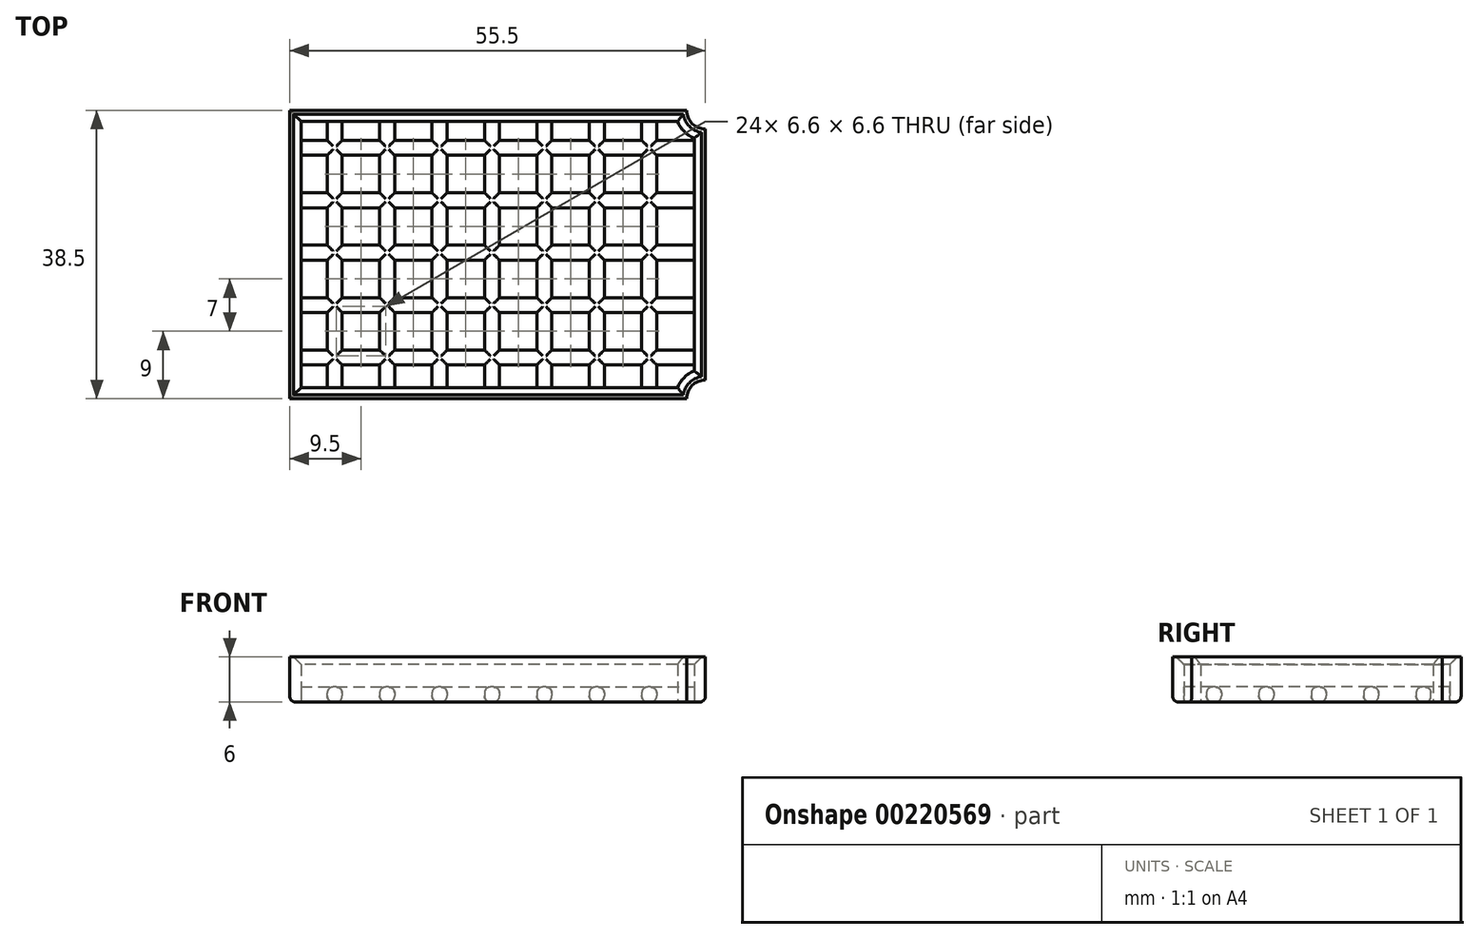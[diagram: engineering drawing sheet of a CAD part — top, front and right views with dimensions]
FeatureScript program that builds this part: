
annotation { "Feature Type Name" : "Feature", "Feature Type Description" : "" }
export const myFeature = defineFeature(function(context is Context, id is Id, definition is map)
    precondition{}
    {
        {
            var Q0;
            Q0=qCreatedBy(makeId("Top.planeOp"),FACE);
            var sketch = newSketch(context, id + "F0", { "sketchPlane" : qUnion([Q0])});
            skLineSegment(sketch, "E0.bottom", {"start": v(0, 38.5) * mm, "end": v(55.5, 38.5) * mm});
            skLineSegment(sketch, "E0.top", {"start": v(0, 0) * mm, "end": v(55.5, 0) * mm});
            skLineSegment(sketch, "E0.left", {"start": v(0, 38.5) * mm, "end": v(0, 0) * mm});
            skLineSegment(sketch, "E0.right", {"start": v(55.5, 38.5) * mm, "end": v(55.5, 0) * mm});
            skSolve(sketch);
        }
        {
            var Q0;
            Q0=qSketchRegion(id+"F0",true);
            extrude(context, id + "F1", {"entities" : qUnion([Q0]), "oppositeDirection" : true, "depth" : 2 * mm});
        }
        {
            var Q0;
            Q0=makeQuery(id+"F1.opExtrude","CAP_FACE",FACE,{"disambiguationData":[OSD([sQuery(id+"F0.wireOp",EDGE,"E0.bottom"),sQuery(id+"F0.wireOp",EDGE,"E0.top"),sQuery(id+"F0.wireOp",EDGE,"E0.left"),sQuery(id+"F0.wireOp",EDGE,"E0.right")])],"isStart":true});
            var sketch = newSketch(context, id + "F2", { "sketchPlane" : qUnion([Q0])});
            skLineSegment(sketch, "E1.bottom", {"start": v(0, 39.5) * mm, "end": v(5, 39.5) * mm});
            skLineSegment(sketch, "E1.top", {"start": v(0, 34.5) * mm, "end": v(5, 34.5) * mm});
            skLineSegment(sketch, "E1.left", {"start": v(0, 39.5) * mm, "end": v(0, 34.5) * mm});
            skLineSegment(sketch, "E1.right", {"start": v(5, 39.5) * mm, "end": v(5, 34.5) * mm});
            skLineSegment(sketch, "E2.0.1.0", {"start": v(0, 32.5) * mm, "end": v(5, 32.5) * mm});
            skLineSegment(sketch, "E2.0.1.1", {"start": v(0, 27.5) * mm, "end": v(5, 27.5) * mm});
            skLineSegment(sketch, "E2.0.1.2", {"start": v(0, 32.5) * mm, "end": v(0, 27.5) * mm});
            skLineSegment(sketch, "E2.0.1.3", {"start": v(5, 32.5) * mm, "end": v(5, 27.5) * mm});
            skLineSegment(sketch, "E2.0.2.0", {"start": v(0, 25.5) * mm, "end": v(5, 25.5) * mm});
            skLineSegment(sketch, "E2.0.2.1", {"start": v(0, 20.5) * mm, "end": v(5, 20.5) * mm});
            skLineSegment(sketch, "E2.0.2.2", {"start": v(0, 25.5) * mm, "end": v(0, 20.5) * mm});
            skLineSegment(sketch, "E2.0.2.3", {"start": v(5, 25.5) * mm, "end": v(5, 20.5) * mm});
            skLineSegment(sketch, "E2.0.3.0", {"start": v(0, 18.5) * mm, "end": v(5, 18.5) * mm});
            skLineSegment(sketch, "E2.0.3.1", {"start": v(0, 13.5) * mm, "end": v(5, 13.5) * mm});
            skLineSegment(sketch, "E2.0.3.2", {"start": v(0, 18.5) * mm, "end": v(0, 13.5) * mm});
            skLineSegment(sketch, "E2.0.3.3", {"start": v(5, 18.5) * mm, "end": v(5, 13.5) * mm});
            skLineSegment(sketch, "E2.0.4.0", {"start": v(0, 11.5) * mm, "end": v(5, 11.5) * mm});
            skLineSegment(sketch, "E2.0.4.1", {"start": v(0, 6.5) * mm, "end": v(5, 6.5) * mm});
            skLineSegment(sketch, "E2.0.4.2", {"start": v(0, 11.5) * mm, "end": v(0, 6.5) * mm});
            skLineSegment(sketch, "E2.0.4.3", {"start": v(5, 11.5) * mm, "end": v(5, 6.5) * mm});
            skLineSegment(sketch, "E2.0.5.0", {"start": v(0, 4.5) * mm, "end": v(5, 4.5) * mm});
            skLineSegment(sketch, "E2.0.5.1", {"start": v(0, -0.5) * mm, "end": v(5, -0.5) * mm});
            skLineSegment(sketch, "E2.0.5.2", {"start": v(0, 4.5) * mm, "end": v(0, -0.5) * mm});
            skLineSegment(sketch, "E2.0.5.3", {"start": v(5, 4.5) * mm, "end": v(5, -0.5) * mm});
            skLineSegment(sketch, "E2.1.0.0", {"start": v(7, 39.5) * mm, "end": v(12, 39.5) * mm});
            skLineSegment(sketch, "E2.1.0.1", {"start": v(7, 34.5) * mm, "end": v(12, 34.5) * mm});
            skLineSegment(sketch, "E2.1.0.2", {"start": v(7, 39.5) * mm, "end": v(7, 34.5) * mm});
            skLineSegment(sketch, "E2.1.0.3", {"start": v(12, 39.5) * mm, "end": v(12, 34.5) * mm});
            skLineSegment(sketch, "E2.1.1.0", {"start": v(7, 32.5) * mm, "end": v(12, 32.5) * mm});
            skLineSegment(sketch, "E2.1.1.1", {"start": v(7, 27.5) * mm, "end": v(12, 27.5) * mm});
            skLineSegment(sketch, "E2.1.1.2", {"start": v(7, 32.5) * mm, "end": v(7, 27.5) * mm});
            skLineSegment(sketch, "E2.1.1.3", {"start": v(12, 32.5) * mm, "end": v(12, 27.5) * mm});
            skLineSegment(sketch, "E2.1.2.0", {"start": v(7, 25.5) * mm, "end": v(12, 25.5) * mm});
            skLineSegment(sketch, "E2.1.2.1", {"start": v(7, 20.5) * mm, "end": v(12, 20.5) * mm});
            skLineSegment(sketch, "E2.1.2.2", {"start": v(7, 25.5) * mm, "end": v(7, 20.5) * mm});
            skLineSegment(sketch, "E2.1.2.3", {"start": v(12, 25.5) * mm, "end": v(12, 20.5) * mm});
            skLineSegment(sketch, "E2.1.3.0", {"start": v(7, 18.5) * mm, "end": v(12, 18.5) * mm});
            skLineSegment(sketch, "E2.1.3.1", {"start": v(7, 13.5) * mm, "end": v(12, 13.5) * mm});
            skLineSegment(sketch, "E2.1.3.2", {"start": v(7, 18.5) * mm, "end": v(7, 13.5) * mm});
            skLineSegment(sketch, "E2.1.3.3", {"start": v(12, 18.5) * mm, "end": v(12, 13.5) * mm});
            skLineSegment(sketch, "E2.1.4.0", {"start": v(7, 11.5) * mm, "end": v(12, 11.5) * mm});
            skLineSegment(sketch, "E2.1.4.1", {"start": v(7, 6.5) * mm, "end": v(12, 6.5) * mm});
            skLineSegment(sketch, "E2.1.4.2", {"start": v(7, 11.5) * mm, "end": v(7, 6.5) * mm});
            skLineSegment(sketch, "E2.1.4.3", {"start": v(12, 11.5) * mm, "end": v(12, 6.5) * mm});
            skLineSegment(sketch, "E2.1.5.0", {"start": v(7, 4.5) * mm, "end": v(12, 4.5) * mm});
            skLineSegment(sketch, "E2.1.5.1", {"start": v(7, -0.5) * mm, "end": v(12, -0.5) * mm});
            skLineSegment(sketch, "E2.1.5.2", {"start": v(7, 4.5) * mm, "end": v(7, -0.5) * mm});
            skLineSegment(sketch, "E2.1.5.3", {"start": v(12, 4.5) * mm, "end": v(12, -0.5) * mm});
            skLineSegment(sketch, "E2.2.0.0", {"start": v(14, 39.5) * mm, "end": v(19, 39.5) * mm});
            skLineSegment(sketch, "E2.2.0.1", {"start": v(14, 34.5) * mm, "end": v(19, 34.5) * mm});
            skLineSegment(sketch, "E2.2.0.2", {"start": v(14, 39.5) * mm, "end": v(14, 34.5) * mm});
            skLineSegment(sketch, "E2.2.0.3", {"start": v(19, 39.5) * mm, "end": v(19, 34.5) * mm});
            skLineSegment(sketch, "E2.2.1.0", {"start": v(14, 32.5) * mm, "end": v(19, 32.5) * mm});
            skLineSegment(sketch, "E2.2.1.1", {"start": v(14, 27.5) * mm, "end": v(19, 27.5) * mm});
            skLineSegment(sketch, "E2.2.1.2", {"start": v(14, 32.5) * mm, "end": v(14, 27.5) * mm});
            skLineSegment(sketch, "E2.2.1.3", {"start": v(19, 32.5) * mm, "end": v(19, 27.5) * mm});
            skLineSegment(sketch, "E2.2.2.0", {"start": v(14, 25.5) * mm, "end": v(19, 25.5) * mm});
            skLineSegment(sketch, "E2.2.2.1", {"start": v(14, 20.5) * mm, "end": v(19, 20.5) * mm});
            skLineSegment(sketch, "E2.2.2.2", {"start": v(14, 25.5) * mm, "end": v(14, 20.5) * mm});
            skLineSegment(sketch, "E2.2.2.3", {"start": v(19, 25.5) * mm, "end": v(19, 20.5) * mm});
            skLineSegment(sketch, "E2.2.3.0", {"start": v(14, 18.5) * mm, "end": v(19, 18.5) * mm});
            skLineSegment(sketch, "E2.2.3.1", {"start": v(14, 13.5) * mm, "end": v(19, 13.5) * mm});
            skLineSegment(sketch, "E2.2.3.2", {"start": v(14, 18.5) * mm, "end": v(14, 13.5) * mm});
            skLineSegment(sketch, "E2.2.3.3", {"start": v(19, 18.5) * mm, "end": v(19, 13.5) * mm});
            skLineSegment(sketch, "E2.2.4.0", {"start": v(14, 11.5) * mm, "end": v(19, 11.5) * mm});
            skLineSegment(sketch, "E2.2.4.1", {"start": v(14, 6.5) * mm, "end": v(19, 6.5) * mm});
            skLineSegment(sketch, "E2.2.4.2", {"start": v(14, 11.5) * mm, "end": v(14, 6.5) * mm});
            skLineSegment(sketch, "E2.2.4.3", {"start": v(19, 11.5) * mm, "end": v(19, 6.5) * mm});
            skLineSegment(sketch, "E2.2.5.0", {"start": v(14, 4.5) * mm, "end": v(19, 4.5) * mm});
            skLineSegment(sketch, "E2.2.5.1", {"start": v(14, -0.5) * mm, "end": v(19, -0.5) * mm});
            skLineSegment(sketch, "E2.2.5.2", {"start": v(14, 4.5) * mm, "end": v(14, -0.5) * mm});
            skLineSegment(sketch, "E2.2.5.3", {"start": v(19, 4.5) * mm, "end": v(19, -0.5) * mm});
            skLineSegment(sketch, "E2.3.0.0", {"start": v(21, 39.5) * mm, "end": v(26, 39.5) * mm});
            skLineSegment(sketch, "E2.3.0.1", {"start": v(21, 34.5) * mm, "end": v(26, 34.5) * mm});
            skLineSegment(sketch, "E2.3.0.2", {"start": v(21, 39.5) * mm, "end": v(21, 34.5) * mm});
            skLineSegment(sketch, "E2.3.0.3", {"start": v(26, 39.5) * mm, "end": v(26, 34.5) * mm});
            skLineSegment(sketch, "E2.3.1.0", {"start": v(21, 32.5) * mm, "end": v(26, 32.5) * mm});
            skLineSegment(sketch, "E2.3.1.1", {"start": v(21, 27.5) * mm, "end": v(26, 27.5) * mm});
            skLineSegment(sketch, "E2.3.1.2", {"start": v(21, 32.5) * mm, "end": v(21, 27.5) * mm});
            skLineSegment(sketch, "E2.3.1.3", {"start": v(26, 32.5) * mm, "end": v(26, 27.5) * mm});
            skLineSegment(sketch, "E2.3.2.0", {"start": v(21, 25.5) * mm, "end": v(26, 25.5) * mm});
            skLineSegment(sketch, "E2.3.2.1", {"start": v(21, 20.5) * mm, "end": v(26, 20.5) * mm});
            skLineSegment(sketch, "E2.3.2.2", {"start": v(21, 25.5) * mm, "end": v(21, 20.5) * mm});
            skLineSegment(sketch, "E2.3.2.3", {"start": v(26, 25.5) * mm, "end": v(26, 20.5) * mm});
            skLineSegment(sketch, "E2.3.3.0", {"start": v(21, 18.5) * mm, "end": v(26, 18.5) * mm});
            skLineSegment(sketch, "E2.3.3.1", {"start": v(21, 13.5) * mm, "end": v(26, 13.5) * mm});
            skLineSegment(sketch, "E2.3.3.2", {"start": v(21, 18.5) * mm, "end": v(21, 13.5) * mm});
            skLineSegment(sketch, "E2.3.3.3", {"start": v(26, 18.5) * mm, "end": v(26, 13.5) * mm});
            skLineSegment(sketch, "E2.3.4.0", {"start": v(21, 11.5) * mm, "end": v(26, 11.5) * mm});
            skLineSegment(sketch, "E2.3.4.1", {"start": v(21, 6.5) * mm, "end": v(26, 6.5) * mm});
            skLineSegment(sketch, "E2.3.4.2", {"start": v(21, 11.5) * mm, "end": v(21, 6.5) * mm});
            skLineSegment(sketch, "E2.3.4.3", {"start": v(26, 11.5) * mm, "end": v(26, 6.5) * mm});
            skLineSegment(sketch, "E2.3.5.0", {"start": v(21, 4.5) * mm, "end": v(26, 4.5) * mm});
            skLineSegment(sketch, "E2.3.5.1", {"start": v(21, -0.5) * mm, "end": v(26, -0.5) * mm});
            skLineSegment(sketch, "E2.3.5.2", {"start": v(21, 4.5) * mm, "end": v(21, -0.5) * mm});
            skLineSegment(sketch, "E2.3.5.3", {"start": v(26, 4.5) * mm, "end": v(26, -0.5) * mm});
            skLineSegment(sketch, "E2.4.0.0", {"start": v(28, 39.5) * mm, "end": v(33, 39.5) * mm});
            skLineSegment(sketch, "E2.4.0.1", {"start": v(28, 34.5) * mm, "end": v(33, 34.5) * mm});
            skLineSegment(sketch, "E2.4.0.2", {"start": v(28, 39.5) * mm, "end": v(28, 34.5) * mm});
            skLineSegment(sketch, "E2.4.0.3", {"start": v(33, 39.5) * mm, "end": v(33, 34.5) * mm});
            skLineSegment(sketch, "E2.4.1.0", {"start": v(28, 32.5) * mm, "end": v(33, 32.5) * mm});
            skLineSegment(sketch, "E2.4.1.1", {"start": v(28, 27.5) * mm, "end": v(33, 27.5) * mm});
            skLineSegment(sketch, "E2.4.1.2", {"start": v(28, 32.5) * mm, "end": v(28, 27.5) * mm});
            skLineSegment(sketch, "E2.4.1.3", {"start": v(33, 32.5) * mm, "end": v(33, 27.5) * mm});
            skLineSegment(sketch, "E2.4.2.0", {"start": v(28, 25.5) * mm, "end": v(33, 25.5) * mm});
            skLineSegment(sketch, "E2.4.2.1", {"start": v(28, 20.5) * mm, "end": v(33, 20.5) * mm});
            skLineSegment(sketch, "E2.4.2.2", {"start": v(28, 25.5) * mm, "end": v(28, 20.5) * mm});
            skLineSegment(sketch, "E2.4.2.3", {"start": v(33, 25.5) * mm, "end": v(33, 20.5) * mm});
            skLineSegment(sketch, "E2.4.3.0", {"start": v(28, 18.5) * mm, "end": v(33, 18.5) * mm});
            skLineSegment(sketch, "E2.4.3.1", {"start": v(28, 13.5) * mm, "end": v(33, 13.5) * mm});
            skLineSegment(sketch, "E2.4.3.2", {"start": v(28, 18.5) * mm, "end": v(28, 13.5) * mm});
            skLineSegment(sketch, "E2.4.3.3", {"start": v(33, 18.5) * mm, "end": v(33, 13.5) * mm});
            skLineSegment(sketch, "E2.4.4.0", {"start": v(28, 11.5) * mm, "end": v(33, 11.5) * mm});
            skLineSegment(sketch, "E2.4.4.1", {"start": v(28, 6.5) * mm, "end": v(33, 6.5) * mm});
            skLineSegment(sketch, "E2.4.4.2", {"start": v(28, 11.5) * mm, "end": v(28, 6.5) * mm});
            skLineSegment(sketch, "E2.4.4.3", {"start": v(33, 11.5) * mm, "end": v(33, 6.5) * mm});
            skLineSegment(sketch, "E2.4.5.0", {"start": v(28, 4.5) * mm, "end": v(33, 4.5) * mm});
            skLineSegment(sketch, "E2.4.5.1", {"start": v(28, -0.5) * mm, "end": v(33, -0.5) * mm});
            skLineSegment(sketch, "E2.4.5.2", {"start": v(28, 4.5) * mm, "end": v(28, -0.5) * mm});
            skLineSegment(sketch, "E2.4.5.3", {"start": v(33, 4.5) * mm, "end": v(33, -0.5) * mm});
            skLineSegment(sketch, "E2.5.0.0", {"start": v(35, 39.5) * mm, "end": v(40, 39.5) * mm});
            skLineSegment(sketch, "E2.5.0.1", {"start": v(35, 34.5) * mm, "end": v(40, 34.5) * mm});
            skLineSegment(sketch, "E2.5.0.2", {"start": v(35, 39.5) * mm, "end": v(35, 34.5) * mm});
            skLineSegment(sketch, "E2.5.0.3", {"start": v(40, 39.5) * mm, "end": v(40, 34.5) * mm});
            skLineSegment(sketch, "E2.5.1.0", {"start": v(35, 32.5) * mm, "end": v(40, 32.5) * mm});
            skLineSegment(sketch, "E2.5.1.1", {"start": v(35, 27.5) * mm, "end": v(40, 27.5) * mm});
            skLineSegment(sketch, "E2.5.1.2", {"start": v(35, 32.5) * mm, "end": v(35, 27.5) * mm});
            skLineSegment(sketch, "E2.5.1.3", {"start": v(40, 32.5) * mm, "end": v(40, 27.5) * mm});
            skLineSegment(sketch, "E2.5.2.0", {"start": v(35, 25.5) * mm, "end": v(40, 25.5) * mm});
            skLineSegment(sketch, "E2.5.2.1", {"start": v(35, 20.5) * mm, "end": v(40, 20.5) * mm});
            skLineSegment(sketch, "E2.5.2.2", {"start": v(35, 25.5) * mm, "end": v(35, 20.5) * mm});
            skLineSegment(sketch, "E2.5.2.3", {"start": v(40, 25.5) * mm, "end": v(40, 20.5) * mm});
            skLineSegment(sketch, "E2.5.3.0", {"start": v(35, 18.5) * mm, "end": v(40, 18.5) * mm});
            skLineSegment(sketch, "E2.5.3.1", {"start": v(35, 13.5) * mm, "end": v(40, 13.5) * mm});
            skLineSegment(sketch, "E2.5.3.2", {"start": v(35, 18.5) * mm, "end": v(35, 13.5) * mm});
            skLineSegment(sketch, "E2.5.3.3", {"start": v(40, 18.5) * mm, "end": v(40, 13.5) * mm});
            skLineSegment(sketch, "E2.5.4.0", {"start": v(35, 11.5) * mm, "end": v(40, 11.5) * mm});
            skLineSegment(sketch, "E2.5.4.1", {"start": v(35, 6.5) * mm, "end": v(40, 6.5) * mm});
            skLineSegment(sketch, "E2.5.4.2", {"start": v(35, 11.5) * mm, "end": v(35, 6.5) * mm});
            skLineSegment(sketch, "E2.5.4.3", {"start": v(40, 11.5) * mm, "end": v(40, 6.5) * mm});
            skLineSegment(sketch, "E2.5.5.0", {"start": v(35, 4.5) * mm, "end": v(40, 4.5) * mm});
            skLineSegment(sketch, "E2.5.5.1", {"start": v(35, -0.5) * mm, "end": v(40, -0.5) * mm});
            skLineSegment(sketch, "E2.5.5.2", {"start": v(35, 4.5) * mm, "end": v(35, -0.5) * mm});
            skLineSegment(sketch, "E2.5.5.3", {"start": v(40, 4.5) * mm, "end": v(40, -0.5) * mm});
            skLineSegment(sketch, "E2.6.0.0", {"start": v(42, 39.5) * mm, "end": v(47, 39.5) * mm});
            skLineSegment(sketch, "E2.6.0.1", {"start": v(42, 34.5) * mm, "end": v(47, 34.5) * mm});
            skLineSegment(sketch, "E2.6.0.2", {"start": v(42, 39.5) * mm, "end": v(42, 34.5) * mm});
            skLineSegment(sketch, "E2.6.0.3", {"start": v(47, 39.5) * mm, "end": v(47, 34.5) * mm});
            skLineSegment(sketch, "E2.6.1.0", {"start": v(42, 32.5) * mm, "end": v(47, 32.5) * mm});
            skLineSegment(sketch, "E2.6.1.1", {"start": v(42, 27.5) * mm, "end": v(47, 27.5) * mm});
            skLineSegment(sketch, "E2.6.1.2", {"start": v(42, 32.5) * mm, "end": v(42, 27.5) * mm});
            skLineSegment(sketch, "E2.6.1.3", {"start": v(47, 32.5) * mm, "end": v(47, 27.5) * mm});
            skLineSegment(sketch, "E2.6.2.0", {"start": v(42, 25.5) * mm, "end": v(47, 25.5) * mm});
            skLineSegment(sketch, "E2.6.2.1", {"start": v(42, 20.5) * mm, "end": v(47, 20.5) * mm});
            skLineSegment(sketch, "E2.6.2.2", {"start": v(42, 25.5) * mm, "end": v(42, 20.5) * mm});
            skLineSegment(sketch, "E2.6.2.3", {"start": v(47, 25.5) * mm, "end": v(47, 20.5) * mm});
            skLineSegment(sketch, "E2.6.3.0", {"start": v(42, 18.5) * mm, "end": v(47, 18.5) * mm});
            skLineSegment(sketch, "E2.6.3.1", {"start": v(42, 13.5) * mm, "end": v(47, 13.5) * mm});
            skLineSegment(sketch, "E2.6.3.2", {"start": v(42, 18.5) * mm, "end": v(42, 13.5) * mm});
            skLineSegment(sketch, "E2.6.3.3", {"start": v(47, 18.5) * mm, "end": v(47, 13.5) * mm});
            skLineSegment(sketch, "E2.6.4.0", {"start": v(42, 11.5) * mm, "end": v(47, 11.5) * mm});
            skLineSegment(sketch, "E2.6.4.1", {"start": v(42, 6.5) * mm, "end": v(47, 6.5) * mm});
            skLineSegment(sketch, "E2.6.4.2", {"start": v(42, 11.5) * mm, "end": v(42, 6.5) * mm});
            skLineSegment(sketch, "E2.6.4.3", {"start": v(47, 11.5) * mm, "end": v(47, 6.5) * mm});
            skLineSegment(sketch, "E2.6.5.0", {"start": v(42, 4.5) * mm, "end": v(47, 4.5) * mm});
            skLineSegment(sketch, "E2.6.5.1", {"start": v(42, -0.5) * mm, "end": v(47, -0.5) * mm});
            skLineSegment(sketch, "E2.6.5.2", {"start": v(42, 4.5) * mm, "end": v(42, -0.5) * mm});
            skLineSegment(sketch, "E2.6.5.3", {"start": v(47, 4.5) * mm, "end": v(47, -0.5) * mm});
            skLineSegment(sketch, "E2.7.0.0", {"start": v(49, 39.5) * mm, "end": v(54, 39.5) * mm});
            skLineSegment(sketch, "E2.7.0.1", {"start": v(49, 34.5) * mm, "end": v(54, 34.5) * mm});
            skLineSegment(sketch, "E2.7.0.2", {"start": v(49, 39.5) * mm, "end": v(49, 34.5) * mm});
            skLineSegment(sketch, "E2.7.0.3", {"start": v(54, 39.5) * mm, "end": v(54, 34.5) * mm});
            skLineSegment(sketch, "E2.7.1.0", {"start": v(49, 32.5) * mm, "end": v(54, 32.5) * mm});
            skLineSegment(sketch, "E2.7.1.1", {"start": v(49, 27.5) * mm, "end": v(54, 27.5) * mm});
            skLineSegment(sketch, "E2.7.1.2", {"start": v(49, 32.5) * mm, "end": v(49, 27.5) * mm});
            skLineSegment(sketch, "E2.7.1.3", {"start": v(54, 32.5) * mm, "end": v(54, 27.5) * mm});
            skLineSegment(sketch, "E2.7.2.0", {"start": v(49, 25.5) * mm, "end": v(54, 25.5) * mm});
            skLineSegment(sketch, "E2.7.2.1", {"start": v(49, 20.5) * mm, "end": v(54, 20.5) * mm});
            skLineSegment(sketch, "E2.7.2.2", {"start": v(49, 25.5) * mm, "end": v(49, 20.5) * mm});
            skLineSegment(sketch, "E2.7.2.3", {"start": v(54, 25.5) * mm, "end": v(54, 20.5) * mm});
            skLineSegment(sketch, "E2.7.3.0", {"start": v(49, 18.5) * mm, "end": v(54, 18.5) * mm});
            skLineSegment(sketch, "E2.7.3.1", {"start": v(49, 13.5) * mm, "end": v(54, 13.5) * mm});
            skLineSegment(sketch, "E2.7.3.2", {"start": v(49, 18.5) * mm, "end": v(49, 13.5) * mm});
            skLineSegment(sketch, "E2.7.3.3", {"start": v(54, 18.5) * mm, "end": v(54, 13.5) * mm});
            skLineSegment(sketch, "E2.7.4.0", {"start": v(49, 11.5) * mm, "end": v(54, 11.5) * mm});
            skLineSegment(sketch, "E2.7.4.1", {"start": v(49, 6.5) * mm, "end": v(54, 6.5) * mm});
            skLineSegment(sketch, "E2.7.4.2", {"start": v(49, 11.5) * mm, "end": v(49, 6.5) * mm});
            skLineSegment(sketch, "E2.7.4.3", {"start": v(54, 11.5) * mm, "end": v(54, 6.5) * mm});
            skLineSegment(sketch, "E2.7.5.0", {"start": v(49, 4.5) * mm, "end": v(54, 4.5) * mm});
            skLineSegment(sketch, "E2.7.5.1", {"start": v(49, -0.5) * mm, "end": v(54, -0.5) * mm});
            skLineSegment(sketch, "E2.7.5.2", {"start": v(49, 4.5) * mm, "end": v(49, -0.5) * mm});
            skLineSegment(sketch, "E2.7.5.3", {"start": v(54, 4.5) * mm, "end": v(54, -0.5) * mm});
            skLineSegment(sketch, "E2.direction1", {"start": v(0, 34.5) * mm, "end": v(7, 34.5) * mm, "construction": true});
            skLineSegment(sketch, "E2.direction2", {"start": v(0, 34.5) * mm, "end": v(0, 27.5) * mm, "construction": true});
            skLineSegment(sketch, "E3.bottom", {"start": v(54, 39.5) * mm, "end": v(58.15, 39.5) * mm});
            skLineSegment(sketch, "E3.top", {"start": v(54, 34.5) * mm, "end": v(58.15, 34.5) * mm});
            skLineSegment(sketch, "E3.right", {"start": v(58.15, 39.5) * mm, "end": v(58.15, 34.5) * mm});
            skLineSegment(sketch, "E4.1.0.0", {"start": v(54, 27.5) * mm, "end": v(58.15, 27.5) * mm});
            skLineSegment(sketch, "E4.1.0.1", {"start": v(58.15, 32.5) * mm, "end": v(58.15, 27.5) * mm});
            skLineSegment(sketch, "E4.1.0.2", {"start": v(54, 32.5) * mm, "end": v(58.15, 32.5) * mm});
            skLineSegment(sketch, "E4.2.0.0", {"start": v(54, 20.5) * mm, "end": v(58.15, 20.5) * mm});
            skLineSegment(sketch, "E4.2.0.1", {"start": v(58.15, 25.5) * mm, "end": v(58.15, 20.5) * mm});
            skLineSegment(sketch, "E4.2.0.2", {"start": v(54, 25.5) * mm, "end": v(58.15, 25.5) * mm});
            skLineSegment(sketch, "E4.3.0.0", {"start": v(54, 13.5) * mm, "end": v(58.15, 13.5) * mm});
            skLineSegment(sketch, "E4.3.0.1", {"start": v(58.15, 18.5) * mm, "end": v(58.15, 13.5) * mm});
            skLineSegment(sketch, "E4.3.0.2", {"start": v(54, 18.5) * mm, "end": v(58.15, 18.5) * mm});
            skLineSegment(sketch, "E4.4.0.0", {"start": v(54, 6.5) * mm, "end": v(58.15, 6.5) * mm});
            skLineSegment(sketch, "E4.4.0.1", {"start": v(58.15, 11.5) * mm, "end": v(58.15, 6.5) * mm});
            skLineSegment(sketch, "E4.4.0.2", {"start": v(54, 11.5) * mm, "end": v(58.15, 11.5) * mm});
            skLineSegment(sketch, "E4.5.0.0", {"start": v(54, -0.5) * mm, "end": v(58.15, -0.5) * mm});
            skLineSegment(sketch, "E4.5.0.1", {"start": v(58.15, 4.5) * mm, "end": v(58.15, -0.5) * mm});
            skLineSegment(sketch, "E4.5.0.2", {"start": v(54, 4.5) * mm, "end": v(58.15, 4.5) * mm});
            skLineSegment(sketch, "E4.direction1", {"start": v(54, 34.5) * mm, "end": v(54, 27.5) * mm, "construction": true});
            skSolve(sketch);
        }
        {
            var Q0;
            Q0=qSketchRegion(id+"F2",true);
            extrude(context, id + "F3", {"entities" : qUnion([Q0]), "operationType" : NewBodyOperationType.REMOVE, "endBound" : BoundingType.THROUGH_ALL, "oppositeDirection" : true, "depth" : 25 * mm});
        }
        {
            var Q0;
            Q0=makeQuery(id+"F1.opExtrude","CAP_FACE",FACE,{"disambiguationData":[OSD([sQuery(id+"F0.wireOp",EDGE,"E0.bottom"),sQuery(id+"F0.wireOp",EDGE,"E0.top"),sQuery(id+"F0.wireOp",EDGE,"E0.left"),sQuery(id+"F0.wireOp",EDGE,"E0.right")])],"isStart":false});
            var sketch = newSketch(context, id + "F4", { "sketchPlane" : qUnion([Q0])});
            skLineSegment(sketch, "E5.bottom", {"start": v(0, 0) * mm, "end": v(55.5, 0) * mm});
            skLineSegment(sketch, "E5.top", {"start": v(0, -38.5) * mm, "end": v(55.5, -38.5) * mm});
            skLineSegment(sketch, "E5.left", {"start": v(0, 0) * mm, "end": v(0, -38.5) * mm});
            skLineSegment(sketch, "E5.right", {"start": v(55.5, 0) * mm, "end": v(55.5, -38.5) * mm});
            skLineSegment(sketch, "E6.0", {"start": v(1.5, -1.5) * mm, "end": v(1.5, -37) * mm});
            skLineSegment(sketch, "E6.1", {"start": v(1.5, -1.5) * mm, "end": v(54, -1.5) * mm});
            skLineSegment(sketch, "E6.2", {"start": v(54, -1.5) * mm, "end": v(54, -37) * mm});
            skLineSegment(sketch, "E6.3", {"start": v(1.5, -37) * mm, "end": v(54, -37) * mm});
            skSolve(sketch);
        }
        {
            var Q0;
            Q0=makeQuery(id+"F1.opExtrude","CAP_FACE",FACE,{"disambiguationData":[OSD([sQuery(id+"F0.wireOp",EDGE,"E0.bottom"),sQuery(id+"F0.wireOp",EDGE,"E0.top"),sQuery(id+"F0.wireOp",EDGE,"E0.left"),sQuery(id+"F0.wireOp",EDGE,"E0.right")])],"isStart":true});
            var Q1;
            Q1=makeQuery(id+"F1.opExtrude","CAP_FACE",FACE,{"disambiguationData":[OSD([sQuery(id+"F0.wireOp",EDGE,"E0.bottom"),sQuery(id+"F0.wireOp",EDGE,"E0.top"),sQuery(id+"F0.wireOp",EDGE,"E0.left"),sQuery(id+"F0.wireOp",EDGE,"E0.right")])],"isStart":false});
            fillet(context, id + "F5", {"entities" : qUnion([Q0, Q1]), "radius" : 0.8 * mm, "defaultsChanged" : true, "vertexSettings" : [], "allowEdgeOverflow" : false});
        }
        {
            var Q0;
            Q0=qSketchRegion(id+"F4",true);
            extrude(context, id + "F6", {"entities" : qUnion([Q0]), "operationType" : NewBodyOperationType.ADD, "oppositeDirection" : true, "depth" : 6 * mm});
        }
        {
            var Q0;
            Q0=makeQuery(id+"F1.opExtrude","CAP_FACE",FACE,{"disambiguationData":[OSD([sQuery(id+"F0.wireOp",EDGE,"E0.bottom"),sQuery(id+"F0.wireOp",EDGE,"E0.top"),sQuery(id+"F0.wireOp",EDGE,"E0.left"),sQuery(id+"F0.wireOp",EDGE,"E0.right")])],"isStart":false});
            var sketch = newSketch(context, id + "F7", { "sketchPlane" : qUnion([Q0])});
            skArc(sketch, "E7", {"start": v(55.5, -34.5) * mm, "mid": v(52.67, -35.67) * mm, "end": v(51.5, -38.5) * mm});
            skArc(sketch, "E8", {"start": v(55.5, -4) * mm, "mid": v(52.67, -2.83) * mm, "end": v(51.5, 0) * mm});
            skLineSegment(sketch, "E9", {"start": v(55.5, -34.5) * mm, "end": v(55.5, -38.5) * mm});
            skLineSegment(sketch, "E10", {"start": v(55.5, -38.5) * mm, "end": v(51.5, -38.5) * mm});
            skLineSegment(sketch, "E11", {"start": v(55.5, 0) * mm, "end": v(55.5, -4) * mm});
            skLineSegment(sketch, "E12", {"start": v(55.5, 0) * mm, "end": v(51.5, 0) * mm});
            skSolve(sketch);
        }
        {
            var Q0;
            Q0 = qSketchRegion(id + "F7", true);
            var Q1;
            Q1=makeQuery(id+"F6.opExtrude","CAP_FACE",FACE,{"disambiguationData":[OSD([sQuery(id+"F4.wireOp",EDGE,"E5.bottom"),sQuery(id+"F4.wireOp",EDGE,"E5.top"),sQuery(id+"F4.wireOp",EDGE,"E5.left"),sQuery(id+"F4.wireOp",EDGE,"E5.right"),sQuery(id+"F4.wireOp",EDGE,"E6.0"),sQuery(id+"F4.wireOp",EDGE,"E6.1"),sQuery(id+"F4.wireOp",EDGE,"E6.2"),sQuery(id+"F4.wireOp",EDGE,"E6.3")])],"isStart":false});
            extrude(context, id + "F8", {"entities" : qUnion([Q0]), "operationType" : NewBodyOperationType.ADD, "endBound" : BoundingType.UP_TO_SURFACE, "oppositeDirection" : true, "depth" : 25 * mm, "endBoundEntityFace" : qUnion([Q1]), "offsetDistance" : 25 * mm});
        }
        {
            var Q0;
            Q0=makeQuery(id+"F1.opExtrude","CAP_FACE",FACE,{"disambiguationData":[OSD([sQuery(id+"F0.wireOp",EDGE,"E0.bottom"),sQuery(id+"F0.wireOp",EDGE,"E0.top"),sQuery(id+"F0.wireOp",EDGE,"E0.left"),sQuery(id+"F0.wireOp",EDGE,"E0.right")])],"isStart":false});
            var sketch = newSketch(context, id + "F9", { "sketchPlane" : qUnion([Q0])});
            skCircle(sketch, "E13", {"center": v(55.5, -38.5) * mm, "radius": 2.5 * mm});
            skCircle(sketch, "E14", {"center": v(55.5, 0) * mm, "radius": 2.5 * mm});
            skSolve(sketch);
        }
        {
            var Q0;
            Q0 = qSketchRegion(id + "F9", true);
            extrude(context, id + "F10", {"entities" : qUnion([Q0]), "operationType" : NewBodyOperationType.REMOVE, "oppositeDirection" : true, "depth" : 25 * mm, "offsetDistance" : 25 * mm});
        }
        {
            var Q0;
            Q0=makeQuery(id+"F6.opExtrude","CAP_EDGE",EDGE,{"disambiguationData":[OSD([sQuery(id+"F4.wireOp",EDGE,"E6.3")])],"isStart":false});
            var Q1;
            Q1=makeQuery(id+"F6.opExtrude","CAP_EDGE",EDGE,{"disambiguationData":[OSD([sQuery(id+"F4.wireOp",EDGE,"E6.0")])],"isStart":false});
            var Q2;
            Q2=makeQuery(id+"F6.opExtrude","CAP_EDGE",EDGE,{"disambiguationData":[OSD([sQuery(id+"F4.wireOp",EDGE,"E6.1")])],"isStart":false});
            var Q3;
            Q3=makeQuery(id+"F6.opExtrude","CAP_EDGE",EDGE,{"disambiguationData":[OSD([sQuery(id+"F4.wireOp",EDGE,"E6.2")])],"isStart":false});
            var Q4;
            Q4=makeQuery(id+"F8.opExtrude","CAP_EDGE",EDGE,{"disambiguationData":[OSD([sQuery(id+"F7.wireOp",EDGE,"KQQ8OCaS-9vgU-Km4c-0UsO-zgIXvIcxwjAX")])],"isStart":false});
            var Q5;
            Q5=makeQuery(id+"F8.opExtrude","CAP_EDGE",EDGE,{"disambiguationData":[OSD([sQuery(id+"F7.wireOp",EDGE,"k1BO5qFm-j4UH-evhB-4JrQ-v7CON569BGps")])],"isStart":false});
            var Q6;
            Q6=makeQuery(id+"F8.opExtrude","CAP_EDGE",EDGE,{"disambiguationData":[OSD([sQuery(id+"F7.wireOp",EDGE,"E7")])],"isStart":false});
            var Q7;
            Q7=makeQuery(id+"F8.opExtrude","CAP_EDGE",EDGE,{"disambiguationData":[OSD([sQuery(id+"F7.wireOp",EDGE,"E8")])],"isStart":false});
            chamfer(context, id + "F11", {"entities" : qUnion([Q0, Q1, Q2, Q3, Q4, Q5, Q6, Q7]), "width" : 1 * mm, "tangentPropagation" : true});
        }
        {
            var Q0;
            Q0=makeQuery(id+"F6.opExtrude","CAP_EDGE",EDGE,{"disambiguationData":[OSD([sQuery(id+"F4.wireOp",EDGE,"E5.left")])],"isStart":true});
            var Q1;
            Q1=makeQuery(id+"F6.opExtrude","CAP_EDGE",EDGE,{"disambiguationData":[OSD([sQuery(id+"F4.wireOp",EDGE,"E5.bottom")])],"isStart":true});
            var Q2;
            Q2=makeQuery(id+"F6.opExtrude","CAP_EDGE",EDGE,{"disambiguationData":[OSD([sQuery(id+"F4.wireOp",EDGE,"E5.right")])],"isStart":true});
            var Q3;
            Q3=makeQuery(id+"F6.opExtrude","CAP_EDGE",EDGE,{"disambiguationData":[OSD([sQuery(id+"F4.wireOp",EDGE,"E5.top")])],"isStart":true});
            var Q4;
            Q4=makeQuery(id+"F10.boolean.opBoolean","COPY",EDGE,{"derivedFrom":makeQuery(id+"F10.opExtrude","CAP_EDGE",EDGE,{"disambiguationData":[OSD([sQuery(id+"F9.wireOp",EDGE,"E13")])],"isStart":true})});
            var Q5;
            Q5=makeQuery(id+"F10.boolean.opBoolean","COPY",EDGE,{"derivedFrom":makeQuery(id+"F10.opExtrude","CAP_EDGE",EDGE,{"disambiguationData":[OSD([sQuery(id+"F9.wireOp",EDGE,"E14")])],"isStart":true})});
            fillet(context, id + "F12", {"entities" : qUnion([Q0, Q1, Q2, Q3, Q4, Q5]), "radius" : 0.75 * mm, "tangentPropagation" : true, "defaultsChanged" : false, "vertexSettings" : [], "allowEdgeOverflow" : false});
        }
    });
